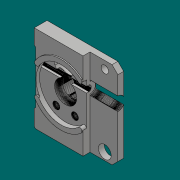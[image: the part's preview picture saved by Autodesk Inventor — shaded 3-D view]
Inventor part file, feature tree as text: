
AUTODESK INVENTOR PART (.ipt)
format: ipt  version: 2018 (Build 220112000, 112)  size: 3,716,608 bytes
history: native  units: mm
features: extrude x20, sketch x20, projected_geometry x7, other x3, fillet x3, chamfer x3
ambient origin geometry x8: Origin, YZ Plane, XZ Plane, XY Plane, X Axis, Y Axis, Z Axis, Center Point
bodies: Body1 (feature_tree)
feature tree (56):
  other  "修復済みジオメトリ1"
  extrude  "押し出し1"  Depth=10.0mm TaperAngle=0.0deg
  extrude  "押し出し2"  Depth=0.5mm TaperAngle=0.0deg
  extrude  "押し出し3"  Depth=10.0mm TaperAngle=0.0deg
  extrude  "押し出し4"  Depth=0.1mm TaperAngle=0.0deg
  extrude  "押し出し5"  Depth=0.1mm TaperAngle=0.0deg
  extrude  "押し出し6"  Depth=2.0mm TaperAngle=0.0deg
  extrude  "押し出し7"  Depth=2.0mm TaperAngle=0.0deg
  extrude  "押し出し8"  Depth=2.0mm TaperAngle=0.0deg
  extrude  "押し出し9"  Depth=0.2mm TaperAngle=0.0deg
  fillet  "フィレット3"  Radius=0.9mm
  extrude  "押し出し10"  Depth=1.0mm TaperAngle=0.0deg
  extrude  "押し出し11"  Depth=8.3mm
  extrude  "押し出し12"  Depth=2.1mm TaperAngle=0.0deg
  extrude  "押し出し13"  Depth=0.1mm TaperAngle=0.0deg
  extrude  "押し出し14"  Depth=1.0mm TaperAngle=0.0deg
  chamfer  "面取り1"  Distance=8.0mm
  chamfer  "面取り2"  Distance=5.6mm
  fillet  "フィレット4"  Radius=1.0mm
  extrude  "押し出し15"  Depth=3.0mm TaperAngle=45.0deg
  fillet  "フィレット5"  Radius=0.2mm
  extrude  "押し出し17"  Depth=1.0mm
  chamfer  "面取り3"  Distance=0.5mm
  extrude  "押し出し18"  Depth=0.6mm
  extrude  "押し出し19"  Depth=1.0mm TaperAngle=0.0deg
  extrude  "押し出し20"  Depth=2.0mm
  extrude  "押し出し21"  Depth=1.6mm
  other  "メッシュ フィーチャ1"
  sketch  "スケッチ1"
  projected_geometry  "投影ループ1"
  sketch  "スケッチ2"
  projected_geometry  "投影ループ2"
  projected_geometry  "投影ループ3"
  sketch  "スケッチ3"
  projected_geometry  "投影ループ4"
  projected_geometry  "投影ループ5"
  sketch  "スケッチ5"
  sketch  "スケッチ6"
  sketch  "スケッチ7"
  sketch  "スケッチ8"
  sketch  "スケッチ9"
  sketch  "スケッチ12"
  sketch  "スケッチ13"
  sketch  "スケッチ14"
  sketch  "スケッチ15"
  sketch  "スケッチ16"
  projected_geometry  "投影ループ7"
  sketch  "スケッチ17"
  sketch  "スケッチ18"
  sketch  "スケッチ20"
  sketch  "スケッチ22"
  sketch  "スケッチ23"
  sketch  "スケッチ24"
  sketch  "スケッチ26"
  projected_geometry  "投影ループ9"
  other  "Srf1"
